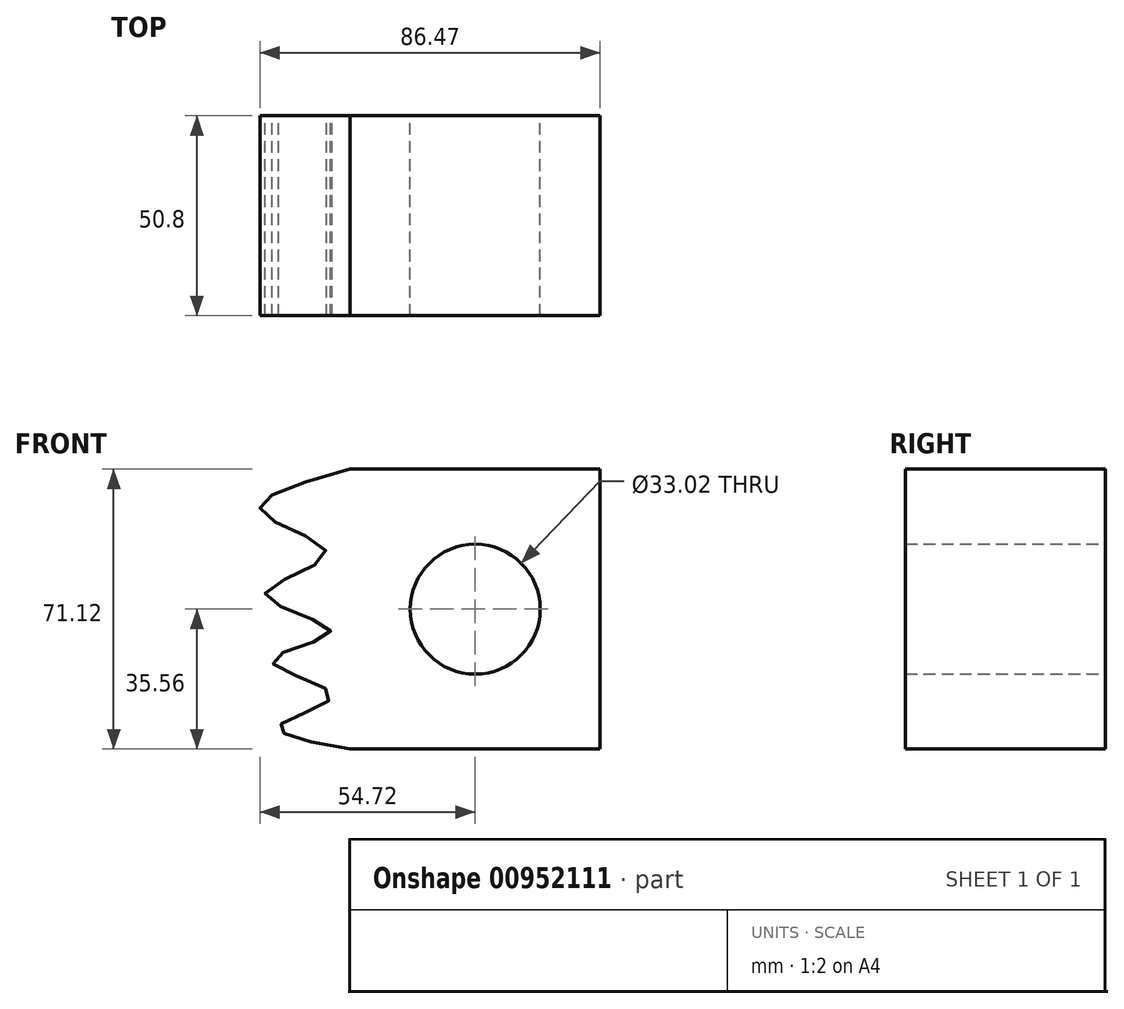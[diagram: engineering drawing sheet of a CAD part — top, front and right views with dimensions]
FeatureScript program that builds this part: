
annotation { "Feature Type Name" : "Feature", "Feature Type Description" : "" }
export const myFeature = defineFeature(function(context is Context, id is Id, definition is map)
    precondition{}
    {
        {
            var Q0;
            Q0=qCreatedBy(makeId("Front.planeOp"),FACE);
            var sketch = newSketch(context, id + "F0", { "sketchPlane" : qUnion([Q0])});
            skLineSegment(sketch, "E0.bottom", {"start": v(31.75, 35.56) * mm, "end": v(-31.75, 35.56) * mm});
            skLineSegment(sketch, "E0.top", {"start": v(31.75, -35.56) * mm, "end": v(-31.75, -35.56) * mm});
            skLineSegment(sketch, "E0.left", {"start": v(31.75, 35.56) * mm, "end": v(31.75, -35.56) * mm});
            skLineSegment(sketch, "E0.right", {"start": v(-31.75, 35.56) * mm, "end": v(-31.75, -35.56) * mm});
            skPoint(sketch, "E0.middle", {"position": v(0, 0) * mm});
            skCircle(sketch, "E1", {"center": v(0, 0) * mm, "radius": 16.51 * mm});
            skFitSpline(sketch, "E2", {"points": [v(-31.75, 35.56) * mm, v(-54.25, 24.6) * mm, v(-37.85, 13.96) * mm, v(-53.39, 3.6) * mm, v(-36.7, -5.61) * mm, v(-51.66, -13.1) * mm, v(-36.4, -21.73) * mm, v(-49.65, -29.5) * mm, v(-31.75, -35.56) * mm], "startDerivative": vector(-280.06, -74.82) * mm, "endDerivative": vector(240.92, -41.95) * mm});
            skSolve(sketch);
        }
        {
            var Q0;
            Q0=makeQuery(id+"F0.imprint","IMPRINT",FACE,{"disambiguationData":[TD([[makeQuery(id+"F0.imprint","IMPRINT",EDGE,{"derivedFrom":sQuery(id+"F0.wireOp",EDGE,"E0.right")}),-1.0]])]});
            var Q1;
            Q1=makeQuery(id+"F0.imprint","IMPRINT",FACE,{"disambiguationData":[TD([[makeQuery(id+"F0.imprint","IMPRINT",EDGE,{"derivedFrom":sQuery(id+"F0.wireOp",EDGE,"E0.bottom")}),1.0]])]});
            extrude(context, id + "F1", {"entities" : qUnion([Q0, Q1]), "endBound" : BoundingType.SYMMETRIC, "depth" : 50.8 * mm, "offsetDistance" : 25.4 * mm});
        }
    });
